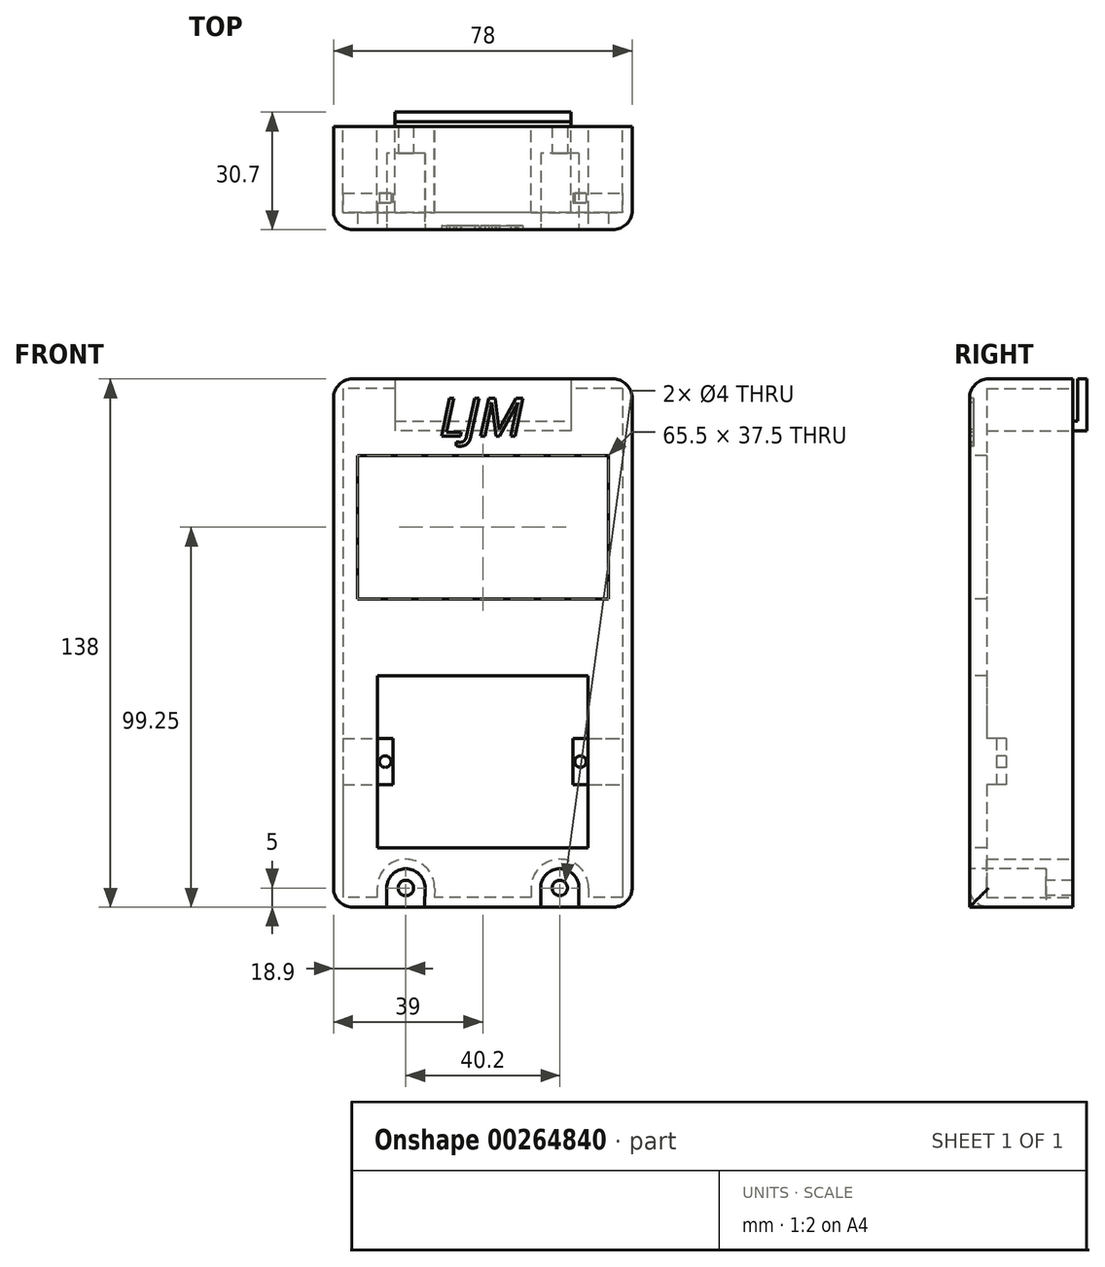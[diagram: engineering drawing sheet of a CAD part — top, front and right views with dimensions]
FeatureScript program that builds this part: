
annotation { "Feature Type Name" : "Feature", "Feature Type Description" : "" }
export const myFeature = defineFeature(function(context is Context, id is Id, definition is map)
    precondition{}
    {
        {
            var Q0;
            Q0=qCreatedBy(makeId("Front.planeOp"),FACE);
            var sketch = newSketch(context, id + "F0", { "sketchPlane" : qUnion([Q0])});
            skLineSegment(sketch, "E0.bottom", {"start": v(39, 69) * mm, "end": v(-39, 69) * mm});
            skLineSegment(sketch, "E0.top", {"start": v(39, -69) * mm, "end": v(-39, -69) * mm});
            skLineSegment(sketch, "E0.left", {"start": v(39, 69) * mm, "end": v(39, -69) * mm});
            skLineSegment(sketch, "E0.right", {"start": v(-39, 69) * mm, "end": v(-39, -69) * mm});
            skPoint(sketch, "E0.middle", {"position": v(0, 0) * mm});
            skLineSegment(sketch, "E1.bottom", {"start": v(32.75, 49) * mm, "end": v(-32.75, 49) * mm});
            skLineSegment(sketch, "E1.top", {"start": v(32.75, 11.5) * mm, "end": v(-32.75, 11.5) * mm});
            skLineSegment(sketch, "E1.left", {"start": v(32.75, 49) * mm, "end": v(32.75, 11.5) * mm});
            skLineSegment(sketch, "E1.right", {"start": v(-32.75, 49) * mm, "end": v(-32.75, 11.5) * mm});
            skPoint(sketch, "E1.middle", {"position": v(0, 30.25) * mm});
            skLineSegment(sketch, "E2.bottom", {"start": v(27.5, -8.5) * mm, "end": v(-27.5, -8.5) * mm});
            skLineSegment(sketch, "E2.top", {"start": v(27.5, -53.5) * mm, "end": v(-27.5, -53.5) * mm});
            skLineSegment(sketch, "E2.left", {"start": v(27.5, -8.5) * mm, "end": v(27.5, -53.5) * mm});
            skLineSegment(sketch, "E2.right", {"start": v(-27.5, -8.5) * mm, "end": v(-27.5, -53.5) * mm});
            skPoint(sketch, "E2.middle", {"position": v(0, -31) * mm});
            skCircle(sketch, "E3", {"center": v(20.1, -64) * mm, "radius": 2 * mm});
            skArc(sketch, "E4", {"start": v(25.1, -64) * mm, "mid": v(20.05, -59) * mm, "end": v(15.1, -64.1) * mm});
            skLineSegment(sketch, "E5", {"start": v(25.1, -64) * mm, "end": v(25.1, -69) * mm});
            skLineSegment(sketch, "E6", {"start": v(15.1, -64.1) * mm, "end": v(15.2, -69) * mm});
            skLineSegment(sketch, "E7.MirrorCS", {"start": v(-25.1, -64) * mm, "end": v(-25.1, -69) * mm});
            skLineSegment(sketch, "E8.MirrorCS", {"start": v(-15.1, -64.1) * mm, "end": v(-15.2, -69) * mm});
            skArc(sketch, "E9.MirrorCS", {"start": v(-25.1, -64) * mm, "mid": v(-20.05, -59) * mm, "end": v(-15.1, -64.1) * mm});
            skCircle(sketch, "E10.MirrorC", {"center": v(-20.1, -64) * mm, "radius": 2 * mm});
            skLineSegment(sketch, "E11.bottom", {"start": v(-23, 69) * mm, "end": v(23, 69) * mm});
            skLineSegment(sketch, "E11.top", {"start": v(-23, 77) * mm, "end": v(23, 77) * mm});
            skLineSegment(sketch, "E11.left", {"start": v(-23, 69) * mm, "end": v(-23, 77) * mm});
            skLineSegment(sketch, "E11.right", {"start": v(23, 69) * mm, "end": v(23, 77) * mm});
            skLineSegment(sketch, "E12.0", {"start": v(12.6, -64.15) * mm, "end": v(12.7, -69.05) * mm});
            skArc(sketch, "E12.1", {"start": v(27.6, -64) * mm, "mid": v(20.02, -56.5) * mm, "end": v(12.6, -64.15) * mm});
            skLineSegment(sketch, "E12.2", {"start": v(27.6, -64) * mm, "end": v(27.6, -69) * mm});
            skLineSegment(sketch, "E13.MirrorCS", {"start": v(-27.6, -64) * mm, "end": v(-27.6, -69) * mm});
            skLineSegment(sketch, "E14.MirrorCS", {"start": v(-12.6, -64.15) * mm, "end": v(-12.7, -69.05) * mm});
            skArc(sketch, "E15.MirrorCS", {"start": v(-27.6, -64) * mm, "mid": v(-20.02, -56.5) * mm, "end": v(-12.6, -64.15) * mm});
            skSolve(sketch);
        }
        {
            var Q0;
            {var subQ0=sQuery(id+"F0.wireOp",EDGE,"E0.left");Q0=makeQuery(id+"F0.imprint","IMPRINT",FACE,{"disambiguationData":[TD([[makeQuery(id+"F0.imprint","IMPRINT",EDGE,{"derivedFrom":subQ0}),-1.0]])]});}
            var Q1;
            Q1=makeQuery(id+"F0.imprint","IMPRINT",FACE,{"disambiguationData":[TD([[makeQuery(id+"F0.imprint","IMPRINT",EDGE,{"derivedFrom":sQuery(id+"F0.wireOp",EDGE,"E3")}),-1.0]])]});
            var Q2;
            {var subQ1=sQuery(id+"F0.wireOp",EDGE,"E7.MirrorCS");Q2=makeQuery(id+"F0.imprint","IMPRINT",FACE,{"disambiguationData":[TD([[makeQuery(id+"F0.imprint","IMPRINT",EDGE,{"derivedFrom":subQ1}),1.0]])]});}
            var Q3;
            Q3=makeQuery(id+"F0.imprint","IMPRINT",FACE,{"disambiguationData":[TD([[makeQuery(id+"F0.imprint","IMPRINT",EDGE,{"derivedFrom":sQuery(id+"F0.wireOp",EDGE,"E4")}),-1.0]])]});
            var Q4;
            {var subQ1=sQuery(id+"F0.wireOp",EDGE,"E7.MirrorCS");Q4=makeQuery(id+"F0.imprint","IMPRINT",FACE,{"disambiguationData":[TD([[makeQuery(id+"F0.imprint","IMPRINT",EDGE,{"derivedFrom":subQ1}),-1.0]])]});}
            extrude(context, id + "F1", {"entities" : qUnion([Q0, Q1, Q2, Q3, Q4]), "oppositeDirection" : true, "depth" : 27 * mm});
        }
        {
            var Q0;
            Q0=makeQuery(id+"F1.opExtrude","CAP_FACE",FACE,{"disambiguationData":[OSD([sQuery(id+"F0.wireOp",EDGE,"E0.bottom"),sQuery(id+"F0.wireOp",EDGE,"E0.top"),sQuery(id+"F0.wireOp",EDGE,"E0.left"),sQuery(id+"F0.wireOp",EDGE,"E0.right"),sQuery(id+"F0.wireOp",EDGE,"E1.bottom"),sQuery(id+"F0.wireOp",EDGE,"E1.top"),sQuery(id+"F0.wireOp",EDGE,"E1.left"),sQuery(id+"F0.wireOp",EDGE,"E1.right"),sQuery(id+"F0.wireOp",EDGE,"E2.bottom"),sQuery(id+"F0.wireOp",EDGE,"E2.top"),sQuery(id+"F0.wireOp",EDGE,"E2.left"),sQuery(id+"F0.wireOp",EDGE,"E2.right"),sQuery(id+"F0.wireOp",EDGE,"E3"),sQuery(id+"F0.wireOp",EDGE,"E10.MirrorC"),sQuery(id+"F0.wireOp",EDGE,"E11.bottom")])],"isStart":false});
            var sketch = newSketch(context, id + "F2", { "sketchPlane" : qUnion([Q0])});
            skLineSegment(sketch, "E16.bottom", {"start": v(-39, 69) * mm, "end": v(39, 69) * mm});
            skLineSegment(sketch, "E16.top", {"start": v(-39, -69) * mm, "end": v(39, -69) * mm});
            skLineSegment(sketch, "E16.left", {"start": v(-39, 69) * mm, "end": v(-39, -69) * mm});
            skLineSegment(sketch, "E16.right", {"start": v(39, 69) * mm, "end": v(39, -69) * mm});
            skLineSegment(sketch, "E17.0", {"start": v(-36.5, 66.5) * mm, "end": v(36.5, 66.5) * mm});
            skLineSegment(sketch, "E17.1", {"start": v(-36.5, 66.5) * mm, "end": v(-36.5, -66.5) * mm});
            skLineSegment(sketch, "E17.2", {"start": v(-36.5, -66.5) * mm, "end": v(36.5, -66.5) * mm});
            skLineSegment(sketch, "E17.3", {"start": v(36.5, 66.5) * mm, "end": v(36.5, -66.5) * mm});
            skLineSegment(sketch, "E18.bottom", {"start": v(-23, 69) * mm, "end": v(23, 69) * mm});
            skArc(sketch, "E19", {"start": v(25.1, -64) * mm, "mid": v(20.05, -59) * mm, "end": v(15.1, -64.1) * mm});
            skLineSegment(sketch, "E20", {"start": v(25.1, -64) * mm, "end": v(25.1, -69) * mm});
            skLineSegment(sketch, "E21", {"start": v(15.1, -64.1) * mm, "end": v(15.2, -69) * mm});
            skLineSegment(sketch, "E22.MirrorCS", {"start": v(-25.1, -64) * mm, "end": v(-25.1, -69) * mm});
            skLineSegment(sketch, "E23.MirrorCS", {"start": v(-15.1, -64.1) * mm, "end": v(-15.2, -69) * mm});
            skArc(sketch, "E24.MirrorCS", {"start": v(-25.1, -64) * mm, "mid": v(-20.05, -59) * mm, "end": v(-15.1, -64.1) * mm});
            skLineSegment(sketch, "E25.0", {"start": v(12.6, -64.15) * mm, "end": v(12.7, -69.05) * mm});
            skArc(sketch, "E25.1", {"start": v(27.6, -64) * mm, "mid": v(20.02, -56.5) * mm, "end": v(12.6, -64.15) * mm});
            skLineSegment(sketch, "E25.2", {"start": v(27.6, -64) * mm, "end": v(27.6, -69) * mm});
            skLineSegment(sketch, "E26.MirrorCS", {"start": v(-27.6, -64) * mm, "end": v(-27.6, -69) * mm});
            skLineSegment(sketch, "E27.MirrorCS", {"start": v(-12.6, -64.15) * mm, "end": v(-12.7, -69.05) * mm});
            skArc(sketch, "E28.MirrorCS", {"start": v(-27.6, -64) * mm, "mid": v(-20.02, -56.5) * mm, "end": v(-12.6, -64.15) * mm});
            skLineSegment(sketch, "E29", {"start": v(-23, 69) * mm, "end": v(-23, 66.5) * mm});
            skLineSegment(sketch, "E30", {"start": v(23, 69) * mm, "end": v(23, 66.5) * mm});
            skLineSegment(sketch, "E31.bottom", {"start": v(-23, 66.5) * mm, "end": v(23, 66.5) * mm});
            skLineSegment(sketch, "E31.top", {"start": v(-23, 58) * mm, "end": v(23, 58) * mm});
            skLineSegment(sketch, "E31.left", {"start": v(-23, 66.5) * mm, "end": v(-23, 58) * mm});
            skLineSegment(sketch, "E31.right", {"start": v(23, 66.5) * mm, "end": v(23, 58) * mm});
            skLineSegment(sketch, "E32.top", {"start": v(-23, 55.5) * mm, "end": v(23, 55.5) * mm});
            skLineSegment(sketch, "E32.left", {"start": v(-23, 58) * mm, "end": v(-23, 55.5) * mm});
            skLineSegment(sketch, "E32.right", {"start": v(23, 58) * mm, "end": v(23, 55.5) * mm});
            skSolve(sketch);
        }
        {
            var Q0;
            Q0=makeQuery(id+"F2.imprint","IMPRINT",FACE,{"disambiguationData":[TD([[makeQuery(id+"F2.imprint","IMPRINT",EDGE,{"derivedFrom":sQuery(id+"F2.wireOp",EDGE,"E31.top")}),-1.0]])]});
            extrude(context, id + "F3", {"entities" : qUnion([Q0]), "depth" : 3.7 * mm});
        }
        {
            var Q0;
            Q0=makeQuery(id+"F2.imprint","IMPRINT",FACE,{"disambiguationData":[TD([[makeQuery(id+"F2.imprint","IMPRINT",EDGE,{"derivedFrom":sQuery(id+"F2.wireOp",EDGE,"E17.0")}),-1.0]])]});
            var Q1;
            Q1 = qSketchRegion(id + "F0", true);
            extrude(context, id + "F4", {"entities" : qUnion([Q0, Q1]), "operationType" : NewBodyOperationType.REMOVE, "oppositeDirection" : true, "depth" : 22.5 * mm});
        }
        {
            var Q0;
            {var subQ1=sQuery(id+"F0.wireOp",EDGE,"E7.MirrorCS");Q0=makeQuery(id+"F0.imprint","IMPRINT",FACE,{"disambiguationData":[TD([[makeQuery(id+"F0.imprint","IMPRINT",EDGE,{"derivedFrom":subQ1}),1.0]])]});}
            var Q1;
            Q1=makeQuery(id+"F0.imprint","IMPRINT",FACE,{"disambiguationData":[TD([[makeQuery(id+"F0.imprint","IMPRINT",EDGE,{"derivedFrom":sQuery(id+"F0.wireOp",EDGE,"E3")}),-1.0]])]});
            extrude(context, id + "F5", {"entities" : qUnion([Q0, Q1]), "operationType" : NewBodyOperationType.REMOVE, "oppositeDirection" : true, "depth" : 20 * mm});
        }
        {
            var Q0;
            Q0=makeQuery(id+"F1.opExtrude","SWEPT_EDGE",EDGE,{"disambiguationData":[OSD([sQuery(id+"F0.wireOp",EDGE,"E0.bottom"),sQuery(id+"F0.wireOp",EDGE,"E0.left")])]});
            var Q1;
            Q1=makeQuery(id+"F1.opExtrude","CAP_EDGE",EDGE,{"disambiguationData":[OSD([sQuery(id+"F0.wireOp",EDGE,"E0.left")])],"isStart":true});
            var Q2;
            Q2=makeQuery(id+"F1.opExtrude","CAP_EDGE",EDGE,{"disambiguationData":[OSD([sQuery(id+"F0.wireOp",EDGE,"E0.bottom"),sQuery(id+"F0.wireOp",EDGE,"E11.bottom")])],"isStart":true});
            var Q3;
            Q3=makeQuery(id+"F1.opExtrude","CAP_EDGE",EDGE,{"disambiguationData":[OSD([sQuery(id+"F0.wireOp",EDGE,"E0.right")])],"isStart":true});
            var Q4;
            {var subQ0=sQuery(id+"F0.wireOp",EDGE,"E0.right");var subQ1=sQuery(id+"F0.wireOp",EDGE,"E0.top");Q4=makeQuery(id+"F5.boolean.opBoolean","SPLIT",EDGE,{"disambiguationData":[TD([makeQuery(id+"F1.opExtrude","SWEPT_FACE",FACE,{"disambiguationData":[OSD([subQ0])]})])],"derivedFrom":makeQuery(id+"F1.opExtrude","CAP_EDGE",EDGE,{"disambiguationData":[OSD([subQ1])],"isStart":true})});}
            var Q5;
            {var subQ0=sQuery(id+"F0.wireOp",EDGE,"E0.top");Q5=makeQuery(id+"F5.boolean.opBoolean","SPLIT",EDGE,{"disambiguationData":[TD([makeQuery(id+"F5.opExtrude","SWEPT_FACE",FACE,{"disambiguationData":[OSD([sQuery(id+"F0.wireOp",EDGE,"E6")])]})])],"derivedFrom":makeQuery(id+"F1.opExtrude","CAP_EDGE",EDGE,{"disambiguationData":[OSD([subQ0])],"isStart":true})});}
            var Q6;
            Q6=makeQuery(id+"F1.opExtrude","SWEPT_EDGE",EDGE,{"disambiguationData":[OSD([sQuery(id+"F0.wireOp",EDGE,"E0.top"),sQuery(id+"F0.wireOp",EDGE,"E0.left")])]});
            var Q7;
            Q7=makeQuery(id+"F1.opExtrude","SWEPT_EDGE",EDGE,{"disambiguationData":[OSD([sQuery(id+"F0.wireOp",EDGE,"E0.top"),sQuery(id+"F0.wireOp",EDGE,"E0.right")])]});
            var Q8;
            Q8=makeQuery(id+"F1.opExtrude","SWEPT_EDGE",EDGE,{"disambiguationData":[OSD([sQuery(id+"F0.wireOp",EDGE,"E0.bottom"),sQuery(id+"F0.wireOp",EDGE,"E0.right")])]});
            fillet(context, id + "F6", {"entities" : qUnion([Q0, Q1, Q2, Q3, Q4, Q5, Q6, Q7, Q8]), "radius" : 5 * mm, "tangentPropagation" : true, "allowEdgeOverflow" : false});
        }
        {
            var Q0;
            Q0=makeQuery(id+"F1.opExtrude","CAP_FACE",FACE,{"disambiguationData":[OSD([sQuery(id+"F0.wireOp",EDGE,"E0.bottom"),sQuery(id+"F0.wireOp",EDGE,"E0.top"),sQuery(id+"F0.wireOp",EDGE,"E0.left"),sQuery(id+"F0.wireOp",EDGE,"E0.right"),sQuery(id+"F0.wireOp",EDGE,"E1.bottom"),sQuery(id+"F0.wireOp",EDGE,"E1.top"),sQuery(id+"F0.wireOp",EDGE,"E1.left"),sQuery(id+"F0.wireOp",EDGE,"E1.right"),sQuery(id+"F0.wireOp",EDGE,"E2.bottom"),sQuery(id+"F0.wireOp",EDGE,"E2.top"),sQuery(id+"F0.wireOp",EDGE,"E2.left"),sQuery(id+"F0.wireOp",EDGE,"E2.right"),sQuery(id+"F0.wireOp",EDGE,"E3"),sQuery(id+"F0.wireOp",EDGE,"E10.MirrorC"),sQuery(id+"F0.wireOp",EDGE,"E11.bottom")])],"isStart":true});
            var sketch = newSketch(context, id + "F7", { "sketchPlane" : qUnion([Q0])});
            skText(sketch, "E33", { "text": "LJM", "fontName": "OpenSans-Italic.ttf"});
            const initialGuessF7  = {"E33": [-0.0114, 0.05403, 1, 0, 0.00997]};
            skSetInitialGuess(sketch, initialGuessF7);
            skSolve(sketch);
        }
        {
            var Q0;
            Q0 = qSketchRegion(id + "F7", true);
            extrude(context, id + "F8", {"entities" : qUnion([Q0]), "operationType" : NewBodyOperationType.REMOVE, "oppositeDirection" : true, "depth" : 1 * mm});
        }
        {
            var Q0;
            Q0=makeQuery(id+"F3.opExtrude","SWEPT_FACE",FACE,{"disambiguationData":[OSD([sQuery(id+"F2.wireOp",EDGE,"E31.top")])]});
            var sketch = newSketch(context, id + "F9", { "sketchPlane" : qUnion([Q0])});
            skLineSegment(sketch, "E34.bottom", {"start": v(-23, 30.7) * mm, "end": v(23, 30.7) * mm});
            skLineSegment(sketch, "E34.top", {"start": v(-23, 28.2) * mm, "end": v(23, 28.2) * mm});
            skLineSegment(sketch, "E34.left", {"start": v(-23, 30.7) * mm, "end": v(-23, 28.2) * mm});
            skLineSegment(sketch, "E34.right", {"start": v(23, 30.7) * mm, "end": v(23, 28.2) * mm});
            skSolve(sketch);
        }
        {
            var Q0;
            Q0=makeQuery(id+"F9.imprint","IMPRINT",FACE,{"disambiguationData":[TD([[makeQuery(id+"F9.imprint","IMPRINT",EDGE,{"derivedFrom":sQuery(id+"F9.wireOp",EDGE,"E34.bottom")}),1.0]])]});
            var Q1;
            Q1=makeQuery(id+"F1.opExtrude","SWEPT_FACE",FACE,{"disambiguationData":[OSD([sQuery(id+"F0.wireOp",EDGE,"E0.bottom"),sQuery(id+"F0.wireOp",EDGE,"E11.bottom")])]});
            extrude(context, id + "F10", {"entities" : qUnion([Q0]), "operationType" : NewBodyOperationType.ADD, "endBound" : BoundingType.UP_TO_SURFACE, "endBoundEntityFace" : qUnion([Q1]), "depth" : 25 * mm});
        }
        {
            var Q0;
            Q0=makeQuery(id+"F4.boolean.opBoolean","COPY",FACE,{"derivedFrom":makeQuery(id+"F4.opExtrude","CAP_FACE",FACE,{"disambiguationData":[OSD([sQuery(id+"F0.wireOp",EDGE,"E1.bottom"),sQuery(id+"F0.wireOp",EDGE,"E1.top"),sQuery(id+"F0.wireOp",EDGE,"E1.left"),sQuery(id+"F0.wireOp",EDGE,"E1.right"),sQuery(id+"F0.wireOp",EDGE,"E2.bottom"),sQuery(id+"F0.wireOp",EDGE,"E2.top"),sQuery(id+"F0.wireOp",EDGE,"E2.left"),sQuery(id+"F0.wireOp",EDGE,"E2.right"),sQuery(id+"F2.wireOp",EDGE,"E17.0"),sQuery(id+"F2.wireOp",EDGE,"E17.1"),sQuery(id+"F2.wireOp",EDGE,"E17.2"),sQuery(id+"F2.wireOp",EDGE,"E17.3"),sQuery(id+"F2.wireOp",EDGE,"E25.0"),sQuery(id+"F2.wireOp",EDGE,"E25.1"),sQuery(id+"F2.wireOp",EDGE,"E25.2"),sQuery(id+"F2.wireOp",EDGE,"E26.MirrorCS"),sQuery(id+"F2.wireOp",EDGE,"E27.MirrorCS"),sQuery(id+"F2.wireOp",EDGE,"E28.MirrorCS"),sQuery(id+"F2.wireOp",EDGE,"E31.left"),sQuery(id+"F2.wireOp",EDGE,"E31.right"),sQuery(id+"F2.wireOp",EDGE,"E32.top"),sQuery(id+"F2.wireOp",EDGE,"E32.left"),sQuery(id+"F2.wireOp",EDGE,"E32.right")])],"isStart":false})});
            var sketch = newSketch(context, id + "F11", { "sketchPlane" : qUnion([Q0])});
            skLineSegment(sketch, "E35", {"start": v(-27.5, -31) * mm, "end": v(27.5, -31) * mm, "construction": true});
            skLineSegment(sketch, "E36.bottom", {"start": v(-27.5, -25) * mm, "end": v(-23.5, -25) * mm});
            skLineSegment(sketch, "E36.top", {"start": v(-27.5, -37) * mm, "end": v(-23.5, -37) * mm});
            skLineSegment(sketch, "E36.right", {"start": v(-23.5, -25) * mm, "end": v(-23.5, -37) * mm});
            skPoint(sketch, "E36.middle", {"position": v(-25.5, -31) * mm});
            skLineSegment(sketch, "E37", {"start": v(-27.5, -25) * mm, "end": v(-36.5, -25) * mm});
            skLineSegment(sketch, "E38", {"start": v(-27.5, -37) * mm, "end": v(-36.5, -37) * mm});
            skCircle(sketch, "E39", {"center": v(-25.5, -31) * mm, "radius": 1.5 * mm});
            skLineSegment(sketch, "E40.MirrorCS", {"start": v(-23.5, -37) * mm, "end": v(-23.5, -25) * mm});
            skLineSegment(sketch, "E41.MirrorCS", {"start": v(27.5, -37) * mm, "end": v(23.5, -37) * mm});
            skLineSegment(sketch, "E42.MirrorCS", {"start": v(27.5, -25) * mm, "end": v(23.5, -25) * mm});
            skLineSegment(sketch, "E43.MirrorCS", {"start": v(23.5, -37) * mm, "end": v(23.5, -25) * mm});
            skLineSegment(sketch, "E44.MirrorCS", {"start": v(27.5, -25) * mm, "end": v(36.5, -25) * mm});
            skCircle(sketch, "E45.MirrorC", {"center": v(25.5, -31) * mm, "radius": 1.5 * mm});
            skLineSegment(sketch, "E46.MirrorCS", {"start": v(27.5, -37) * mm, "end": v(36.5, -37) * mm});
            skLineSegment(sketch, "E47.MirrorCS", {"start": v(23.5, -25) * mm, "end": v(23.5, -37) * mm});
            skSolve(sketch);
        }
        {
            var Q0;
            {var subQ0=sQuery(id+"F11.wireOp",EDGE,"E38");Q0=makeQuery(id+"F11.imprint","IMPRINT",FACE,{"disambiguationData":[TD([[makeQuery(id+"F11.imprint","IMPRINT",EDGE,{"derivedFrom":subQ0}),-1.0]])]});}
            var Q1;
            {var subQ1=sQuery(id+"F11.wireOp",EDGE,"E36.bottom");Q1=makeQuery(id+"F11.imprint","IMPRINT",FACE,{"disambiguationData":[TD([[makeQuery(id+"F11.imprint","IMPRINT",EDGE,{"derivedFrom":subQ1}),-1.0]])]});}
            var Q2;
            {var subQ1=sQuery(id+"F11.wireOp",EDGE,"E41.MirrorCS");Q2=makeQuery(id+"F11.imprint","IMPRINT",FACE,{"disambiguationData":[TD([[makeQuery(id+"F11.imprint","IMPRINT",EDGE,{"derivedFrom":subQ1}),-1.0]])]});}
            var Q3;
            {var subQ0=sQuery(id+"F11.wireOp",EDGE,"E46.MirrorCS");Q3=makeQuery(id+"F11.imprint","IMPRINT",FACE,{"disambiguationData":[TD([[makeQuery(id+"F11.imprint","IMPRINT",EDGE,{"derivedFrom":subQ0}),1.0]])]});}
            extrude(context, id + "F12", {"entities" : qUnion([Q0, Q1, Q2, Q3]), "operationType" : NewBodyOperationType.ADD, "depth" : 5 * mm});
        }
        {
            var Q0;
            Q0=makeQuery(id+"F12.opExtrude","CAP_FACE",FACE,{"disambiguationData":[OSD([sQuery(id+"F2.wireOp",EDGE,"E17.3"),sQuery(id+"F11.wireOp",EDGE,"E41.MirrorCS"),sQuery(id+"F11.wireOp",EDGE,"E47.MirrorCS"),sQuery(id+"F11.wireOp",EDGE,"E42.MirrorCS"),sQuery(id+"F11.wireOp",EDGE,"E46.MirrorCS"),sQuery(id+"F11.wireOp",EDGE,"E44.MirrorCS"),sQuery(id+"F11.wireOp",EDGE,"E45.MirrorC")])],"isStart":true});
            var Q1;
            Q1=makeQuery(id+"F12.opExtrude","CAP_FACE",FACE,{"disambiguationData":[OSD([sQuery(id+"F2.wireOp",EDGE,"E17.1"),sQuery(id+"F11.wireOp",EDGE,"E36.bottom"),sQuery(id+"F11.wireOp",EDGE,"E40.MirrorCS"),sQuery(id+"F11.wireOp",EDGE,"E38"),sQuery(id+"F11.wireOp",EDGE,"E37"),sQuery(id+"F11.wireOp",EDGE,"E36.top"),sQuery(id+"F11.wireOp",EDGE,"E39")])],"isStart":true});
            extrude(context, id + "F13", {"entities" : qUnion([Q0, Q1]), "operationType" : NewBodyOperationType.REMOVE, "oppositeDirection" : true, "depth" : 2.5 * mm});
        }
    });
